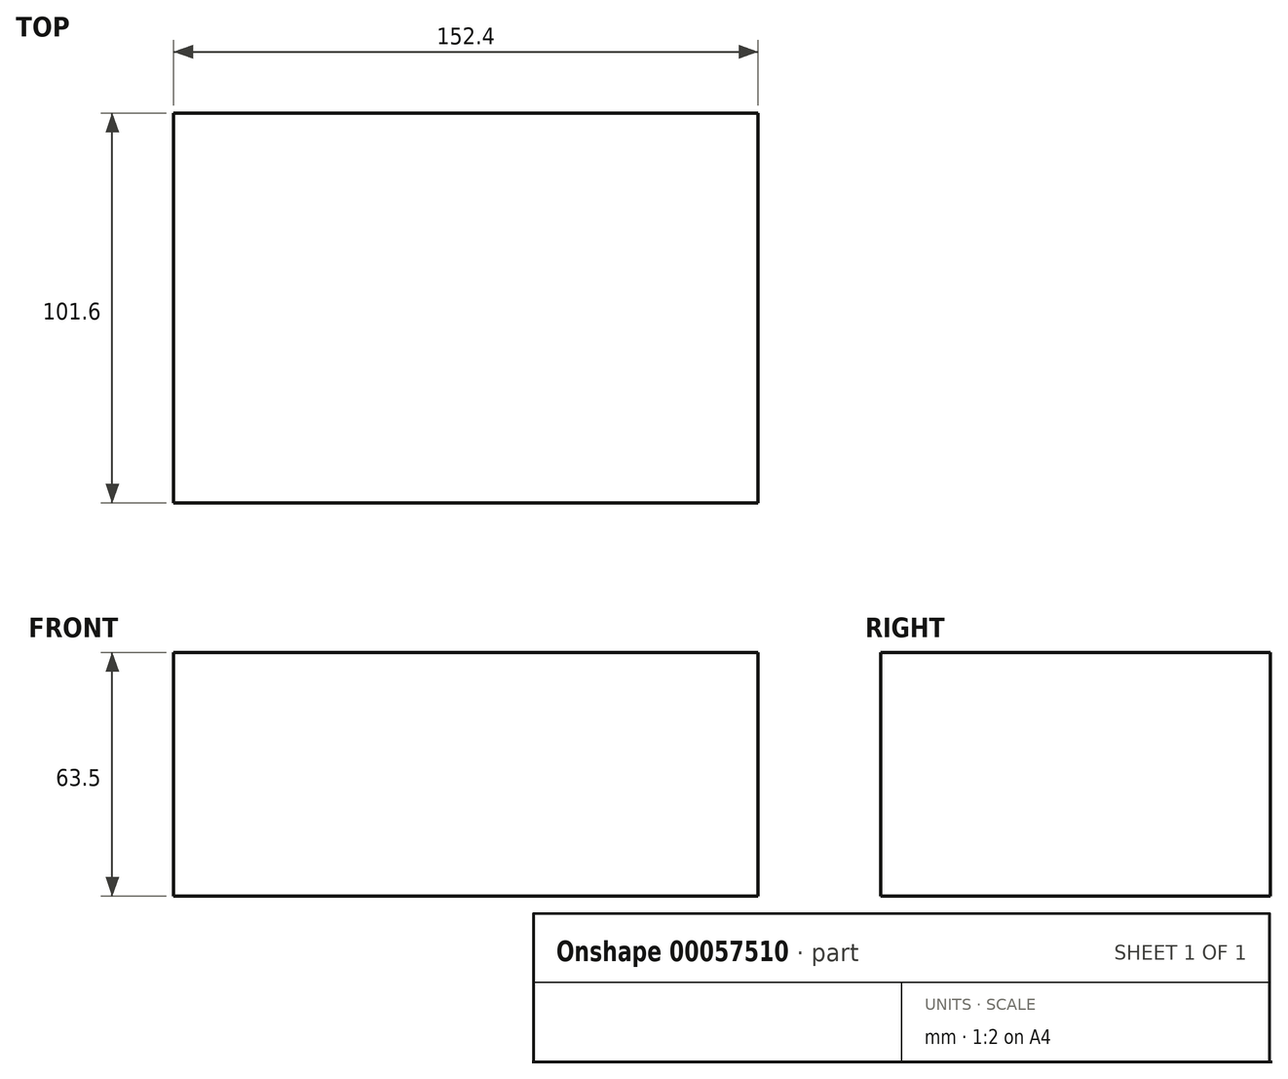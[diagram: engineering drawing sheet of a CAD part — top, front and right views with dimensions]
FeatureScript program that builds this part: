
annotation { "Feature Type Name" : "Feature", "Feature Type Description" : "" }
export const myFeature = defineFeature(function(context is Context, id is Id, definition is map)
    precondition{}
    {
        {
            var Q0;
            Q0=qCreatedBy(makeId("Front.planeOp"),FACE);
            var sketch = newSketch(context, id + "F0", { "sketchPlane" : qUnion([Q0])});
            skLineSegment(sketch, "E0.bottom", {"start": v(-50.8, 50.8) * mm, "end": v(101.6, 50.8) * mm});
            skLineSegment(sketch, "E0.top", {"start": v(-50.8, -12.7) * mm, "end": v(101.6, -12.7) * mm});
            skLineSegment(sketch, "E0.left", {"start": v(-50.8, 50.8) * mm, "end": v(-50.8, -12.7) * mm});
            skLineSegment(sketch, "E0.right", {"start": v(101.6, 50.8) * mm, "end": v(101.6, -12.7) * mm});
            skSolve(sketch);
        }
        {
            var Q0;
            Q0 = qSketchRegion(id + "F0", true);
            extrude(context, id + "F1", {"entities" : qUnion([Q0]), "depth" : 101.6 * mm});
        }
    });
